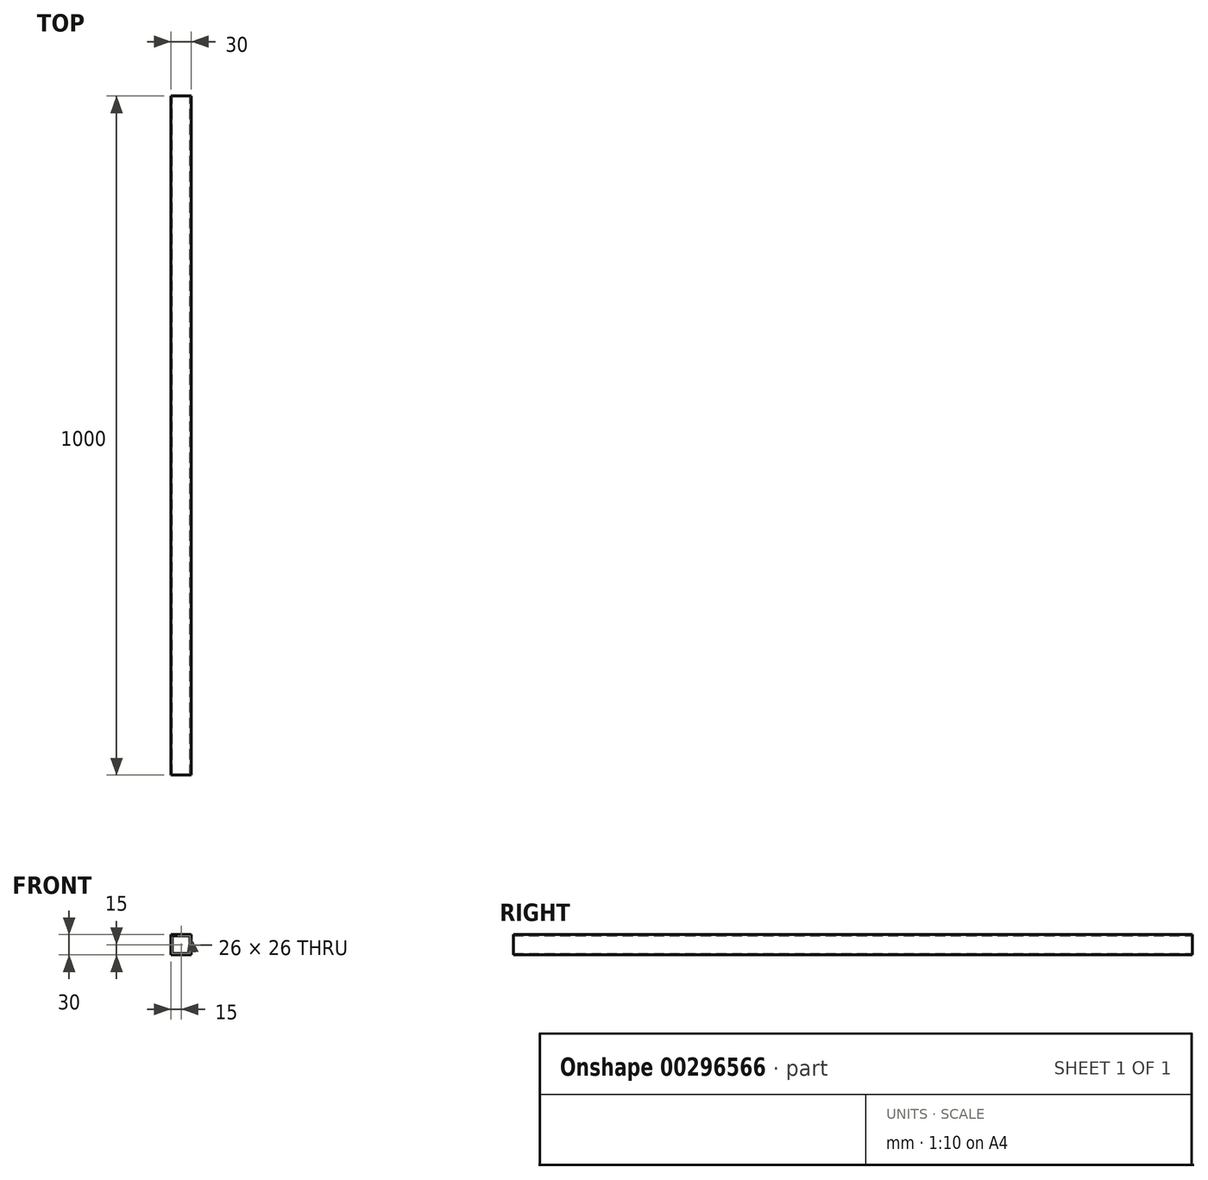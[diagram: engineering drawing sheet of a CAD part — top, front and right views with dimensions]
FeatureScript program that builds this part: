
annotation { "Feature Type Name" : "Feature", "Feature Type Description" : "" }
export const myFeature = defineFeature(function(context is Context, id is Id, definition is map)
    precondition{}
    {
        {
            var Q0;
            Q0=qCreatedBy(makeId("Front.planeOp"),FACE);
            var sketch = newSketch(context, id + "F0", { "sketchPlane" : qUnion([Q0])});
            skLineSegment(sketch, "E0.bottom", {"start": v(15, 15) * mm, "end": v(-15, 15) * mm});
            skLineSegment(sketch, "E0.top", {"start": v(15, -15) * mm, "end": v(-15, -15) * mm});
            skLineSegment(sketch, "E0.left", {"start": v(15, 15) * mm, "end": v(15, -15) * mm});
            skLineSegment(sketch, "E0.right", {"start": v(-15, 15) * mm, "end": v(-15, -15) * mm});
            skPoint(sketch, "E0.middle", {"position": v(0, 0) * mm});
            skLineSegment(sketch, "E1.bottom", {"start": v(13, 13) * mm, "end": v(-13, 13) * mm});
            skLineSegment(sketch, "E1.top", {"start": v(13, -13) * mm, "end": v(-13, -13) * mm});
            skLineSegment(sketch, "E1.left", {"start": v(13, 13) * mm, "end": v(13, -13) * mm});
            skLineSegment(sketch, "E1.right", {"start": v(-13, 13) * mm, "end": v(-13, -13) * mm});
            skSolve(sketch);
        }
        {
            var Q0;
            Q0=makeQuery(id+"F0.imprint","IMPRINT",FACE,{"disambiguationData":[TD([[makeQuery(id+"F0.imprint","IMPRINT",EDGE,{"derivedFrom":sQuery(id+"F0.wireOp",EDGE,"E0.bottom")}),1.0]])]});
            extrude(context, id + "F1", {"entities" : qUnion([Q0]), "depth" : 1000 * mm});
        }
    });
